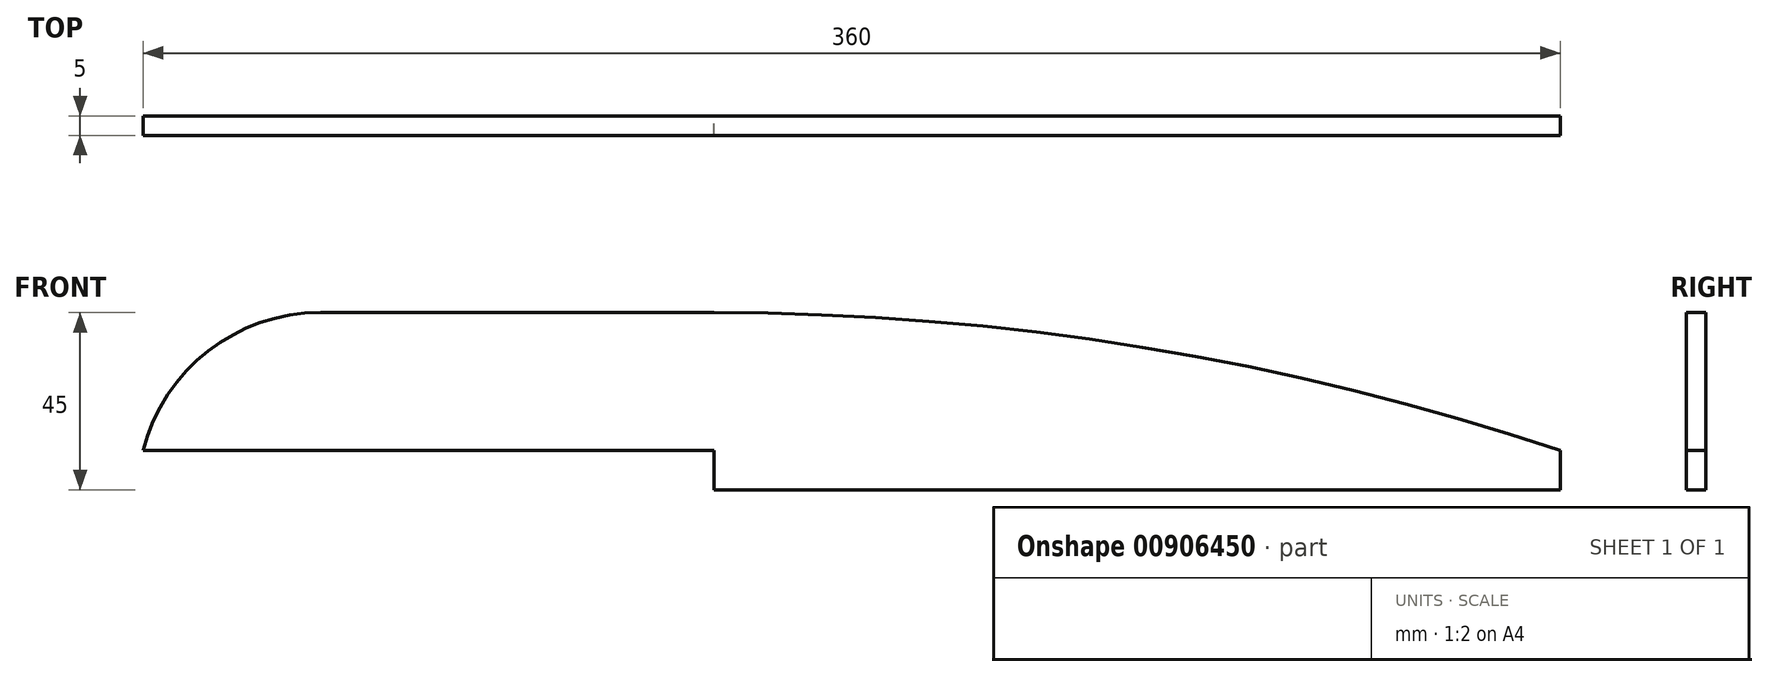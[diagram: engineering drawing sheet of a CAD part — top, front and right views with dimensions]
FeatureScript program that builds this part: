
annotation { "Feature Type Name" : "Feature", "Feature Type Description" : "" }
export const myFeature = defineFeature(function(context is Context, id is Id, definition is map)
    precondition{}
    {
        {
            var Q0;
            Q0=qCreatedBy(makeId("Front.planeOp"),FACE);
            var sketch = newSketch(context, id + "F0", { "sketchPlane" : qUnion([Q0])});
            skLineSegment(sketch, "E0", {"start": v(-145, 10) * mm, "end": v(0, 10) * mm});
            skLineSegment(sketch, "E1", {"start": v(0, 10) * mm, "end": v(0, 0) * mm});
            skLineSegment(sketch, "E2", {"start": v(0, 0) * mm, "end": v(215, 0) * mm});
            skLineSegment(sketch, "E3", {"start": v(215, 0) * mm, "end": v(215, 10) * mm});
            skPoint(sketch, "E4", {"position": v(0, 45) * mm});
            skArc(sketch, "E5", {"start": v(215, 10) * mm, "mid": v(108.92, 36.2) * mm, "end": v(0, 45) * mm});
            skLineSegment(sketch, "E6", {"start": v(0, 45) * mm, "end": v(-100, 45) * mm});
            skArc(sketch, "E7", {"start": v(-100, 45) * mm, "mid": v(-128.5, 35.22) * mm, "end": v(-145, 10) * mm});
            skSolve(sketch);
        }
        {
            var Q0;
            Q0 = qSketchRegion(id + "F0", true);
            extrude(context, id + "F1", {"entities" : qUnion([Q0]), "endBound" : BoundingType.SYMMETRIC, "depth" : 5 * mm, "offsetDistance" : 25 * mm});
        }
    });
